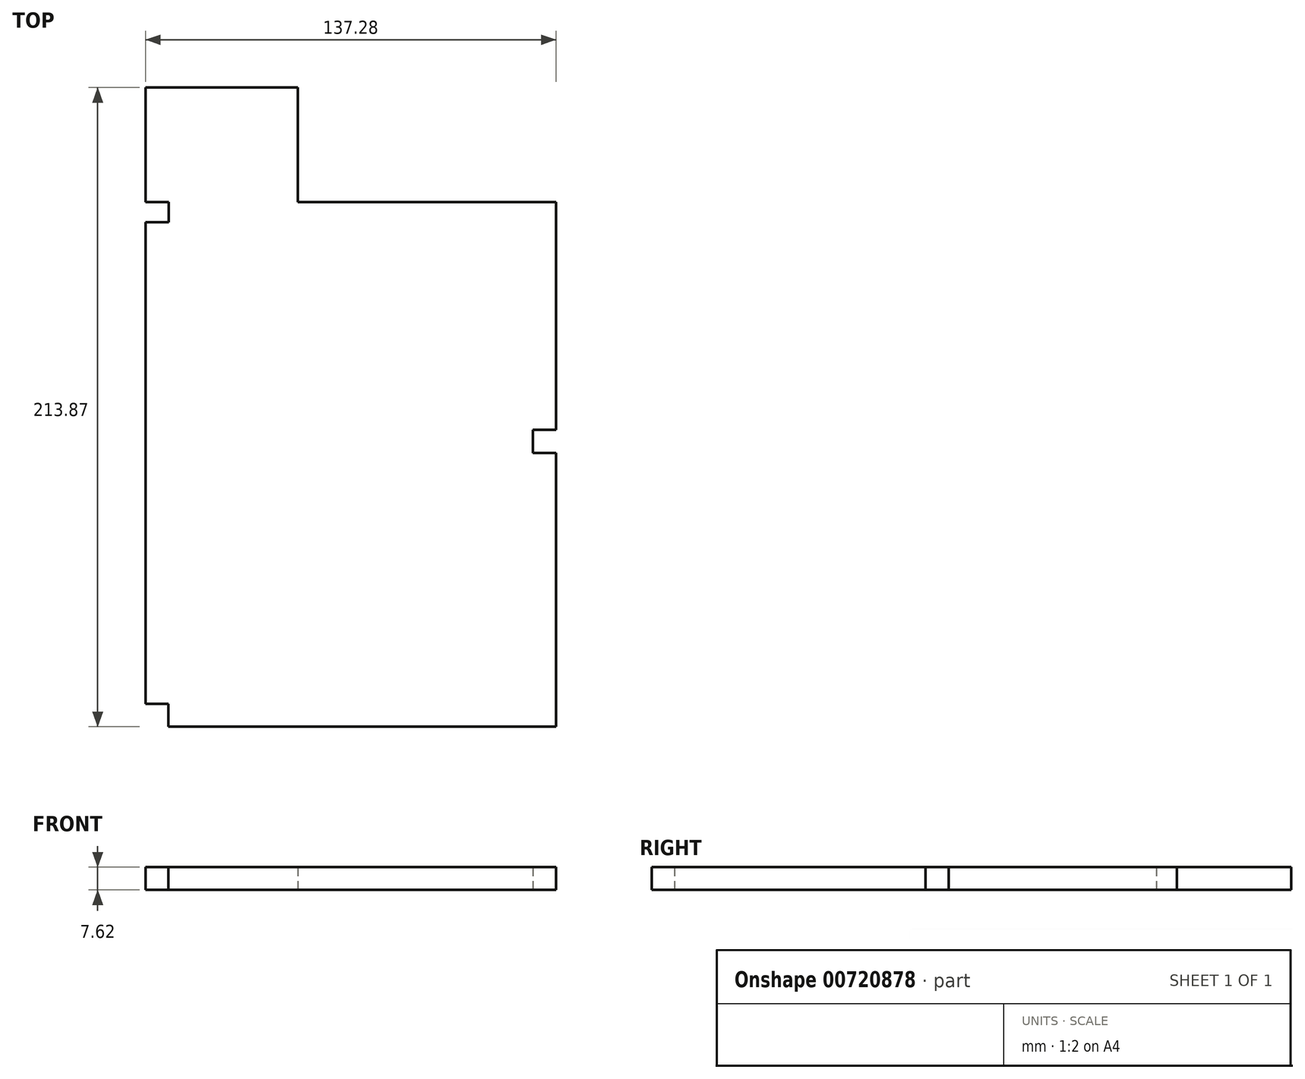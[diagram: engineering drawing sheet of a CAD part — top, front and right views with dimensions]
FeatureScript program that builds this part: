
annotation { "Feature Type Name" : "Feature", "Feature Type Description" : "" }
export const myFeature = defineFeature(function(context is Context, id is Id, definition is map)
    precondition{}
    {
        {
            var Q0;
            Q0=qCreatedBy(makeId("Top.planeOp"),FACE);
            var sketch = newSketch(context, id + "F0", { "sketchPlane" : qUnion([Q0])});
            skLineSegment(sketch, "E0", {"start": v(-62.3, 47.34) * mm, "end": v(-11.37, 47.34) * mm});
            skLineSegment(sketch, "E1", {"start": v(-11.37, 47.34) * mm, "end": v(-11.37, 9.07) * mm});
            skLineSegment(sketch, "E2", {"start": v(-62.3, 9.07) * mm, "end": v(-62.3, 47.34) * mm});
            skLineSegment(sketch, "E3", {"start": v(-11.37, 9.07) * mm, "end": v(74.97, 9.07) * mm});
            skLineSegment(sketch, "E4", {"start": v(74.97, 9.07) * mm, "end": v(74.97, -67.2) * mm});
            skLineSegment(sketch, "E5", {"start": v(74.97, -67.2) * mm, "end": v(67.2, -67.2) * mm});
            skLineSegment(sketch, "E6", {"start": v(67.2, -67.2) * mm, "end": v(67.2, -74.97) * mm});
            skLineSegment(sketch, "E7", {"start": v(67.2, -74.97) * mm, "end": v(74.97, -74.97) * mm});
            skLineSegment(sketch, "E8", {"start": v(74.97, -74.97) * mm, "end": v(74.97, -166.53) * mm});
            skLineSegment(sketch, "E9", {"start": v(74.97, -166.53) * mm, "end": v(-52.08, -166.53) * mm});
            skLineSegment(sketch, "E10", {"start": v(-52.08, -166.53) * mm, "end": v(-54.68, -166.53) * mm});
            skLineSegment(sketch, "E11", {"start": v(-54.68, -166.53) * mm, "end": v(-54.68, -158.86) * mm});
            skLineSegment(sketch, "E12", {"start": v(-54.68, -158.86) * mm, "end": v(-62.31, -158.86) * mm});
            skLineSegment(sketch, "E13", {"start": v(-62.31, -158.86) * mm, "end": v(-62.31, 2.29) * mm});
            skLineSegment(sketch, "E14", {"start": v(-62.31, 2.29) * mm, "end": v(-54.6, 2.29) * mm});
            skLineSegment(sketch, "E15", {"start": v(-54.6, 2.29) * mm, "end": v(-54.6, 9.07) * mm});
            skLineSegment(sketch, "E16", {"start": v(-62.3, 9.07) * mm, "end": v(-54.6, 9.07) * mm});
            skSolve(sketch);
        }
        {
            var Q0;
            Q0 = qSketchRegion(id + "F0", true);
            extrude(context, id + "F1", {"entities" : qUnion([Q0]), "depth" : 7.62 * mm, "offsetDistance" : 25.4 * mm});
        }
    });
